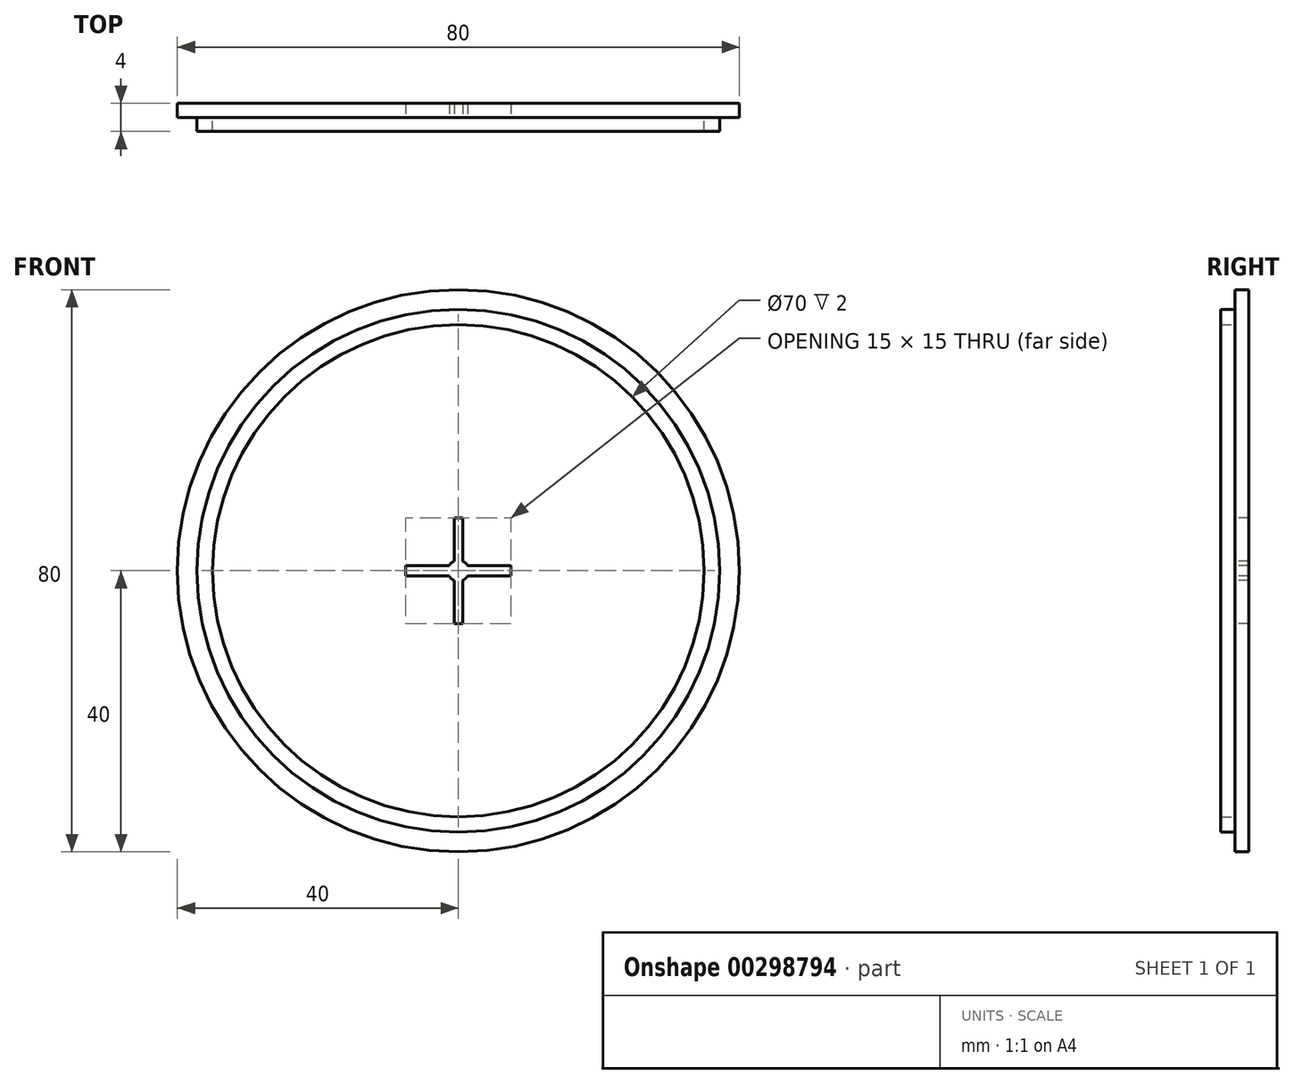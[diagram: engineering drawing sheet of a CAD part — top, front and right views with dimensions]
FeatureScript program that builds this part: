
annotation { "Feature Type Name" : "Feature", "Feature Type Description" : "" }
export const myFeature = defineFeature(function(context is Context, id is Id, definition is map)
    precondition{}
    {
        {
            var Q0;
            Q0=qCreatedBy(makeId("Front.planeOp"),FACE);
            var sketch = newSketch(context, id + "F0", { "sketchPlane" : qUnion([Q0])});
            skCircle(sketch, "E0", {"center": v(0, 0) * mm, "radius": 40 * mm});
            skSolve(sketch);
        }
        {
            var Q0;
            Q0 = qSketchRegion(id + "F0", true);
            extrude(context, id + "F1", {"entities" : qUnion([Q0]), "depth" : 2 * mm});
        }
        {
            var Q0;
            Q0=makeQuery(id+"F1.opExtrude","CAP_FACE",FACE,{"disambiguationData":[OSD([sQuery(id+"F0.wireOp",EDGE,"E0")])],"isStart":false});
            var sketch = newSketch(context, id + "F2", { "sketchPlane" : qUnion([Q0])});
            skCircle(sketch, "E1", {"center": v(0, 0) * mm, "radius": 37.2 * mm});
            skCircle(sketch, "E2", {"center": v(0, 0) * mm, "radius": 35 * mm});
            skSolve(sketch);
        }
        {
            var Q0;
            Q0 = qSketchRegion(id + "F2", true);
            extrude(context, id + "F3", {"entities" : qUnion([Q0]), "operationType" : NewBodyOperationType.ADD, "depth" : 2 * mm});
        }
        {
            var Q0;
            Q0=makeQuery(id+"F3.boolean.opBoolean","SPLIT",FACE,{"disambiguationData":[TD([makeQuery(id+"F3.opExtrude","SWEPT_FACE",FACE,{"disambiguationData":[OSD([sQuery(id+"F2.wireOp",EDGE,"E2")])]})])],"derivedFrom":makeQuery(id+"F1.opExtrude","CAP_FACE",FACE,{"disambiguationData":[OSD([sQuery(id+"F0.wireOp",EDGE,"E0")])],"isStart":false})});
            var sketch = newSketch(context, id + "F4", { "sketchPlane" : qUnion([Q0])});
            skLineSegment(sketch, "E3.bottom", {"start": v(-0.6, 7.5) * mm, "end": v(0.6, 7.5) * mm});
            skLineSegment(sketch, "E3.top", {"start": v(-0.6, -7.5) * mm, "end": v(0.6, -7.5) * mm});
            skLineSegment(sketch, "E3.left", {"start": v(-0.6, 7.5) * mm, "end": v(-0.6, -7.5) * mm});
            skLineSegment(sketch, "E3.right", {"start": v(0.6, 7.5) * mm, "end": v(0.6, -7.5) * mm});
            skPoint(sketch, "E3.middle", {"position": v(0, 0) * mm});
            skLineSegment(sketch, "E4.bottom", {"start": v(-7.5, 0.75) * mm, "end": v(7.5, 0.75) * mm});
            skLineSegment(sketch, "E4.top", {"start": v(-7.5, -0.75) * mm, "end": v(7.5, -0.75) * mm});
            skLineSegment(sketch, "E4.left", {"start": v(-7.5, 0.75) * mm, "end": v(-7.5, -0.75) * mm});
            skLineSegment(sketch, "E4.right", {"start": v(7.5, 0.75) * mm, "end": v(7.5, -0.75) * mm});
            skCircle(sketch, "E5", {"center": v(0, 0) * mm, "radius": 1.5 * mm});
            skSolve(sketch);
        }
        {
            var Q0;
            Q0 = qSketchRegion(id + "F4", true);
            extrude(context, id + "F5", {"entities" : qUnion([Q0]), "operationType" : NewBodyOperationType.REMOVE, "oppositeDirection" : true, "depth" : 25 * mm});
        }
        {
            var Q0;
            {var subQ0=sQuery(id+"F4.wireOp",EDGE,"E4.bottom");var subQ1=sQuery(id+"F4.wireOp",EDGE,"E3.left");var subQ2=makeQuery(id+"F4.imprint","INTERSECT",VERTEX,{"derivedFrom":[subQ1,subQ0]});Q0=makeQuery(id+"F5.boolean.opBoolean","SPLIT",FACE,{"disambiguationData":[TD([makeQuery(id+"F5.opExtrude","SWEPT_FACE",FACE,{"disambiguationData":[OSD([subQ1]),TDD([makeQuery(id+"F4.imprint","IMPRINT",EDGE,{"disambiguationData":[TD([[subQ2,-1.0]])],"derivedFrom":subQ1})])]})])],"derivedFrom":makeQuery(id+"F3.boolean.opBoolean","SPLIT",FACE,{"disambiguationData":[TD([makeQuery(id+"F3.opExtrude","SWEPT_FACE",FACE,{"disambiguationData":[OSD([sQuery(id+"F2.wireOp",EDGE,"E2")])]})])],"derivedFrom":makeQuery(id+"F1.opExtrude","CAP_FACE",FACE,{"disambiguationData":[OSD([sQuery(id+"F0.wireOp",EDGE,"E0")])],"isStart":false})})});}
            extrude(context, id + "F6", {"entities" : qUnion([Q0]), "operationType" : NewBodyOperationType.REMOVE, "oppositeDirection" : true, "depth" : 25 * mm});
        }
    });
